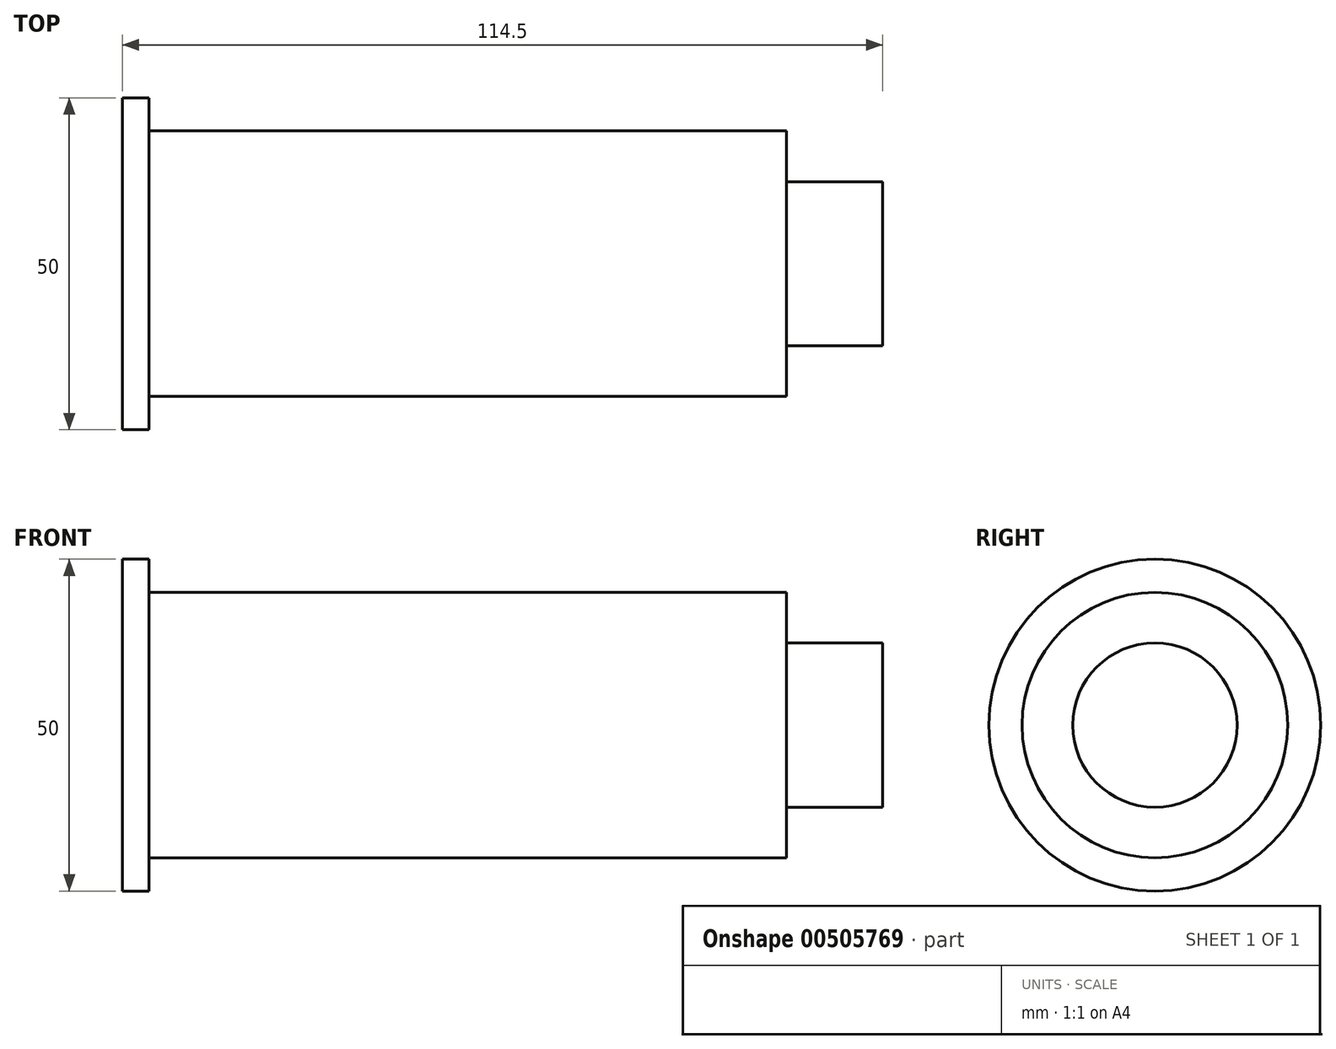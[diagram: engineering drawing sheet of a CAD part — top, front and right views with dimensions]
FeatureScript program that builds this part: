
annotation { "Feature Type Name" : "Feature", "Feature Type Description" : "" }
export const myFeature = defineFeature(function(context is Context, id is Id, definition is map)
    precondition{}
    {
        {
            var Q0;
            Q0=qCreatedBy(makeId("Front.planeOp"),FACE);
            var sketch = newSketch(context, id + "F0", { "sketchPlane" : qUnion([Q0])});
            skLineSegment(sketch, "E0.bottom", {"start": v(0, 0) * mm, "end": v(-100, 0) * mm});
            skLineSegment(sketch, "E0.top", {"start": v(0, 20) * mm, "end": v(-96, 20) * mm});
            skLineSegment(sketch, "E0.left", {"start": v(0, 0) * mm, "end": v(0, 20) * mm});
            skLineSegment(sketch, "E0.right", {"start": v(-100, 0) * mm, "end": v(-100, 20) * mm});
            skLineSegment(sketch, "E1.top", {"start": v(-100, 25) * mm, "end": v(-96, 25) * mm});
            skLineSegment(sketch, "E1.left", {"start": v(-100, 20) * mm, "end": v(-100, 25) * mm});
            skLineSegment(sketch, "E1.right", {"start": v(-96, 20) * mm, "end": v(-96, 25) * mm});
            skSolve(sketch);
        }
        {
            var Q0;
            Q0=makeQuery(id+"F0.imprint","IMPRINT",FACE,{"disambiguationData":[TD([[makeQuery(id+"F0.imprint","IMPRINT",EDGE,{"derivedFrom":sQuery(id+"F0.wireOp",EDGE,"E0.bottom")}),-1.0]])]});
            var Q1;
            Q1=sQuery(id+"F0.wireOp",EDGE,"E0.bottom");
            revolve(context, id + "F1", {"entities" : qUnion([Q0]), "axis" : qUnion([Q1]), "revolveType" : RevolveType.FULL});
        }
        {
            var Q0;
            Q0=makeQuery(id+"F1.opRevolve","SWEPT_FACE",FACE,{"disambiguationData":[OSD([sQuery(id+"F0.wireOp",EDGE,"E0.left")])]});
            var sketch = newSketch(context, id + "F2", { "sketchPlane" : qUnion([Q0])});
            skCircle(sketch, "E2", {"center": v(0, 0) * mm, "radius": 12.37 * mm});
            skSolve(sketch);
        }
        {
            var Q0;
            Q0=qSketchRegion(id+"F2",true);
            extrude(context, id + "F3", {"entities" : qUnion([Q0]), "operationType" : NewBodyOperationType.ADD, "depth" : 14.5 * mm});
        }
    });
